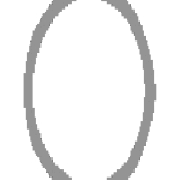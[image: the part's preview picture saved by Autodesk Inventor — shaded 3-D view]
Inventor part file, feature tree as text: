
AUTODESK INVENTOR PART (.ipt)
format: ipt  version: 2021 (Build 250183000, 183)  size: 114,688 bytes
history: native  units: in
note: dims shown in document units (in); Inventor stores cm internally (conversion verified against a paired STEP export)
features: other x4, sketch x3, plane x1
ambient origin geometry x8: Origin, YZ Plane, XZ Plane, XY Plane, X Axis, Y Axis, Z Axis, Center Point
bodies: Solid1 (feature_tree), Body (feature_tree)
feature tree (8):
  other  "Driven Length"
  other  "Frame Generator"
  other  "Start Plane"
  other  "End Plane"
  sketch  "Sketch"  dims[d2=5.831in d4=-0.0in d5=5.831in d6=0.12in d7=0.0in d8=90.0deg d9=5.831in]
  sketch  "Sketch2"  dims[d0=1.0in]
  plane  "Work Plane3"
  sketch  "Sketch3"  dims[d1=0.065in]
